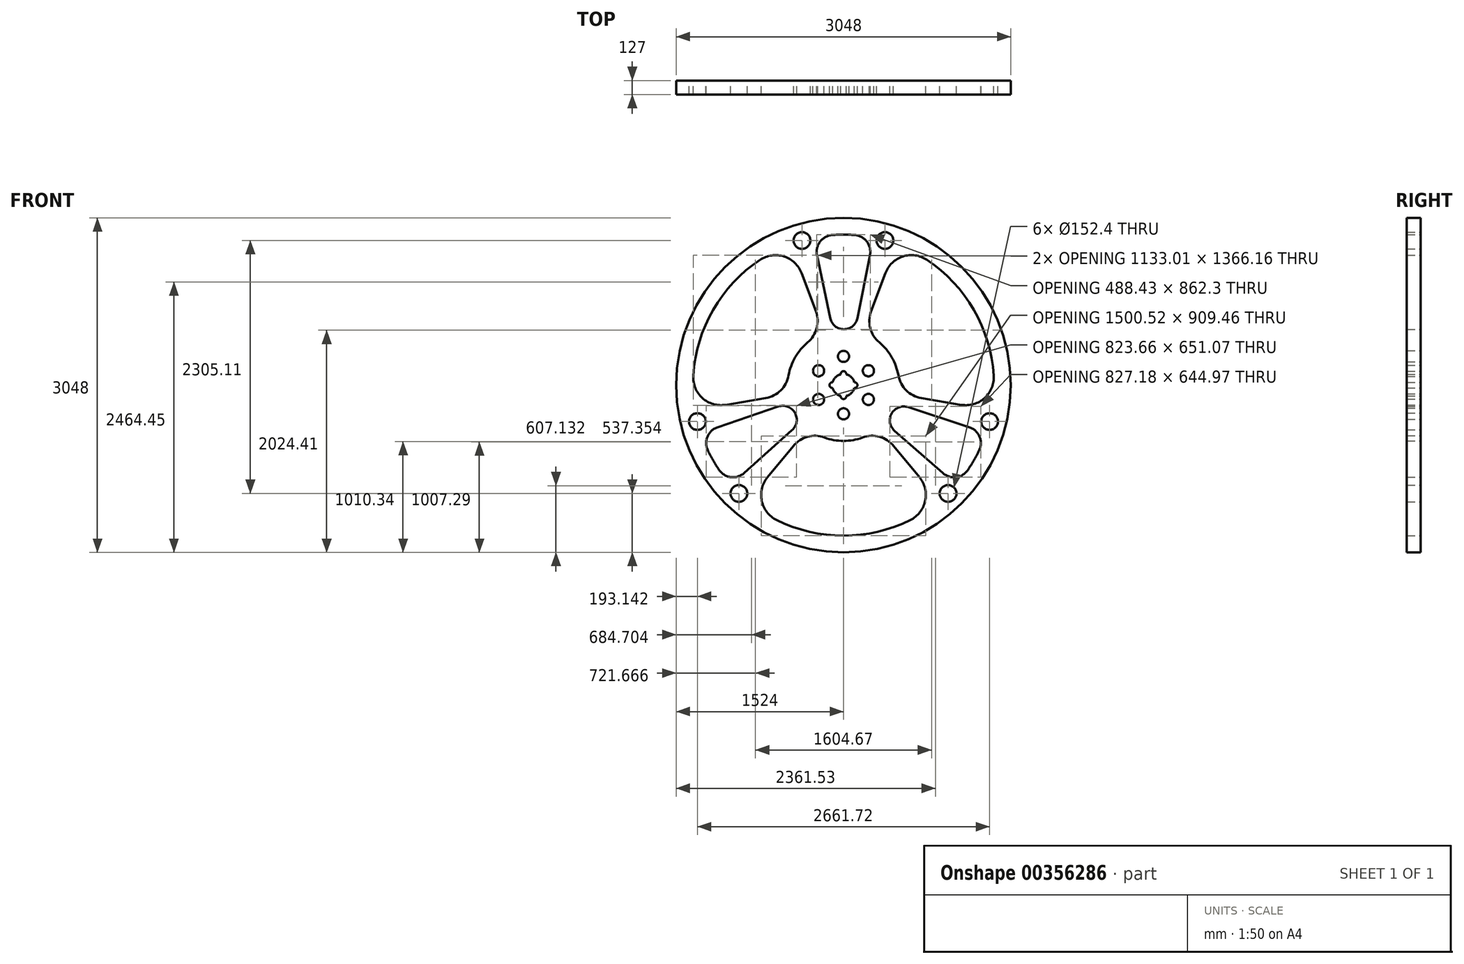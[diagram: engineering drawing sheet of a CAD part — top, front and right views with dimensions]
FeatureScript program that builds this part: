
annotation { "Feature Type Name" : "Feature", "Feature Type Description" : "" }
export const myFeature = defineFeature(function(context is Context, id is Id, definition is map)
    precondition{}
    {
        {
            var Q0;
            Q0=qCreatedBy(makeId("Front.planeOp"),FACE);
            var sketch = newSketch(context, id + "F0", { "sketchPlane" : qUnion([Q0])});
            skCircle(sketch, "E0", {"center": v(0, 0) * mm, "radius": 1524 * mm});
            skCircle(sketch, "E1", {"center": v(0, 0) * mm, "radius": 381 * mm});
            skArc(sketch, "E2", {"start": v(-173.99, -477.28) * mm, "mid": v(0, -508) * mm, "end": v(173.99, -477.28) * mm});
            skArc(sketch, "E3", {"start": v(241.16, 1185.35) * mm, "mid": v(213.39, 1307.65) * mm, "end": v(103.3, 1367.7) * mm});
            skArc(sketch, "E4", {"start": v(-103.3, 1367.7) * mm, "mid": v(-213.39, 1307.65) * mm, "end": v(-241.16, 1185.35) * mm});
            skArc(sketch, "E5", {"start": v(-120.93, 610.98) * mm, "mid": v(3.52, 509.3) * mm, "end": v(127.97, 610.98) * mm});
            skLineSegment(sketch, "E6.trimOffspring", {"start": v(-241.16, 1185.35) * mm, "end": v(-120.93, 610.98) * mm});
            skArc(sketch, "E7.trimOffspring", {"start": v(103.3, 1367.7) * mm, "mid": v(0, 1371.6) * mm, "end": v(-103.3, 1367.7) * mm});
            skLineSegment(sketch, "E8.trimOffspring", {"start": v(241.16, 1185.35) * mm, "end": v(127.97, 610.98) * mm});
            skPoint(sketch, "E9.orphan", {"position": v(0, 1871.22) * mm});
            skPoint(sketch, "E10.start.orphan", {"position": v(380.7, 1871.22) * mm});
            skLineSegment(sketch, "E11.trimOffspring", {"start": v(456.97, -554.35) * mm, "end": v(692.28, -839.8) * mm});
            skLineSegment(sketch, "E12.trimOffspring", {"start": v(-456.97, -554.35) * mm, "end": v(-692.28, -839.8) * mm});
            skArc(sketch, "E13", {"start": v(456.97, -554.35) * mm, "mid": v(327.73, -470.84) * mm, "end": v(173.99, -477.28) * mm});
            skArc(sketch, "E14", {"start": v(-173.99, -477.28) * mm, "mid": v(-327.73, -470.84) * mm, "end": v(-456.97, -554.35) * mm});
            skCircle(sketch, "E15", {"center": v(-378.06, 1318.47) * mm, "radius": 76.2 * mm});
            skCircle(sketch, "E16", {"center": v(378.06, 1318.47) * mm, "radius": 76.2 * mm});
            skArc(sketch, "E17", {"start": v(-609.08, -1228.95) * mm, "mid": v(0, -1371.6) * mm, "end": v(609.08, -1228.95) * mm});
            skArc(sketch, "E18", {"start": v(-692.28, -839.8) * mm, "mid": v(-744.67, -1054.47) * mm, "end": v(-609.08, -1228.95) * mm});
            skArc(sketch, "E19", {"start": v(609.08, -1228.95) * mm, "mid": v(744.67, -1054.47) * mm, "end": v(692.28, -839.8) * mm});
            skArc(sketch, "E20.trimOffspring", {"start": v(1132.82, -773.31) * mm, "mid": v(1187.84, -685.8) * mm, "end": v(1236.12, -594.4) * mm});
            skArc(sketch, "E21.1.0", {"start": v(-1236.12, -594.4) * mm, "mid": v(-1187.84, -685.8) * mm, "end": v(-1132.82, -773.31) * mm});
            skArc(sketch, "E21.1.1", {"start": v(-1132.82, -773.31) * mm, "mid": v(-1025.76, -838.62) * mm, "end": v(-905.96, -801.53) * mm});
            skLineSegment(sketch, "E21.1.2", {"start": v(-905.96, -801.53) * mm, "end": v(-468.66, -410.22) * mm});
            skArc(sketch, "E21.1.3", {"start": v(-468.66, -410.22) * mm, "mid": v(-442.83, -251.6) * mm, "end": v(-593.11, -194.66) * mm});
            skLineSegment(sketch, "E21.1.4", {"start": v(-1147.13, -383.82) * mm, "end": v(-593.11, -194.66) * mm});
            skArc(sketch, "E21.1.5", {"start": v(-1147.13, -383.82) * mm, "mid": v(-1239.15, -469.02) * mm, "end": v(-1236.12, -594.4) * mm});
            skCircle(sketch, "E21.1.6", {"center": v(-1330.86, -331.82) * mm, "radius": 76.2 * mm});
            skCircle(sketch, "E21.1.7", {"center": v(-952.8, -986.65) * mm, "radius": 76.2 * mm});
            skArc(sketch, "E21.2.1", {"start": v(1236.12, -594.4) * mm, "mid": v(1239.15, -469.02) * mm, "end": v(1147.13, -383.82) * mm});
            skLineSegment(sketch, "E21.2.2", {"start": v(1147.13, -383.82) * mm, "end": v(589.59, -200.77) * mm});
            skArc(sketch, "E21.2.3", {"start": v(589.59, -200.77) * mm, "mid": v(439.3, -257.7) * mm, "end": v(465.14, -416.32) * mm});
            skLineSegment(sketch, "E21.2.4", {"start": v(905.96, -801.53) * mm, "end": v(465.14, -416.32) * mm});
            skArc(sketch, "E21.2.5", {"start": v(905.96, -801.53) * mm, "mid": v(1025.76, -838.62) * mm, "end": v(1132.82, -773.31) * mm});
            skCircle(sketch, "E21.2.6", {"center": v(952.8, -986.65) * mm, "radius": 76.2 * mm});
            skCircle(sketch, "E21.2.7", {"center": v(1330.86, -331.82) * mm, "radius": 76.2 * mm});
            skArc(sketch, "E22.1.0", {"start": v(251.6, 672.92) * mm, "mid": v(243.9, 519.24) * mm, "end": v(326.34, 389.31) * mm});
            skArc(sketch, "E22.1.1", {"start": v(500.33, 87.96) * mm, "mid": v(439.94, 254) * mm, "end": v(326.34, 389.31) * mm});
            skArc(sketch, "E22.1.2", {"start": v(500.33, 87.96) * mm, "mid": v(571.62, -48.4) * mm, "end": v(708.57, -118.57) * mm});
            skLineSegment(sketch, "E22.1.3", {"start": v(708.57, -118.57) * mm, "end": v(1073.43, -179.63) * mm});
            skArc(sketch, "E22.1.4", {"start": v(1073.43, -179.63) * mm, "mid": v(1285.53, -117.67) * mm, "end": v(1368.84, 87) * mm});
            skArc(sketch, "E22.1.5", {"start": v(1368.84, 87) * mm, "mid": v(1187.84, 685.8) * mm, "end": v(759.76, 1141.95) * mm});
            skArc(sketch, "E22.1.6", {"start": v(759.76, 1141.95) * mm, "mid": v(540.86, 1172.14) * mm, "end": v(381.15, 1019.43) * mm});
            skLineSegment(sketch, "E22.1.7", {"start": v(251.6, 672.92) * mm, "end": v(381.15, 1019.43) * mm});
            skArc(sketch, "E22.2.0", {"start": v(-708.57, -118.57) * mm, "mid": v(-571.62, -48.4) * mm, "end": v(-500.33, 87.96) * mm});
            skArc(sketch, "E22.2.1", {"start": v(-326.34, 389.31) * mm, "mid": v(-439.94, 254) * mm, "end": v(-500.33, 87.96) * mm});
            skArc(sketch, "E22.2.2", {"start": v(-326.34, 389.31) * mm, "mid": v(-243.9, 519.24) * mm, "end": v(-251.6, 672.92) * mm});
            skLineSegment(sketch, "E22.2.3", {"start": v(-251.6, 672.92) * mm, "end": v(-381.15, 1019.43) * mm});
            skArc(sketch, "E22.2.4", {"start": v(-381.15, 1019.43) * mm, "mid": v(-540.86, 1172.14) * mm, "end": v(-759.76, 1141.95) * mm});
            skArc(sketch, "E22.2.5", {"start": v(-759.76, 1141.95) * mm, "mid": v(-1187.84, 685.8) * mm, "end": v(-1368.84, 87) * mm});
            skArc(sketch, "E22.2.6", {"start": v(-1368.84, 87) * mm, "mid": v(-1285.53, -117.67) * mm, "end": v(-1073.43, -179.63) * mm});
            skLineSegment(sketch, "E22.2.7", {"start": v(-708.57, -118.57) * mm, "end": v(-1073.43, -179.63) * mm});
            skCircle(sketch, "E23", {"center": v(0, 261.86) * mm, "radius": 50.8 * mm});
            skCircle(sketch, "E24.1.0", {"center": v(-226.78, -130.93) * mm, "radius": 50.8 * mm});
            skCircle(sketch, "E24.2.0", {"center": v(226.78, -130.93) * mm, "radius": 50.8 * mm});
            skCircle(sketch, "E25.1.1", {"center": v(0, -261.86) * mm, "radius": 50.8 * mm});
            skCircle(sketch, "E25.1.2", {"center": v(226.78, 130.93) * mm, "radius": 50.8 * mm});
            skCircle(sketch, "E26.4.3.0", {"center": v(-226.78, 130.93) * mm, "radius": 50.8 * mm});
            skCircle(sketch, "E26.2.5.0", {"center": v(-226.78, 130.93) * mm, "radius": 50.8 * mm});
            skArc(sketch, "E27", {"start": v(-25.2, 98.42) * mm, "mid": v(-71.84, 71.84) * mm, "end": v(-98.43, 25.2) * mm});
            skArc(sketch, "E28", {"start": v(-98.43, 25.2) * mm, "mid": v(-127, 0) * mm, "end": v(-98.43, -25.2) * mm});
            skArc(sketch, "E29", {"start": v(98.42, -25.2) * mm, "mid": v(127, 0) * mm, "end": v(98.43, 25.2) * mm});
            skArc(sketch, "E30", {"start": v(25.2, 98.42) * mm, "mid": v(0, 127) * mm, "end": v(-25.2, 98.43) * mm});
            skArc(sketch, "E31", {"start": v(-25.2, -98.42) * mm, "mid": v(0, -127) * mm, "end": v(25.2, -98.43) * mm});
            skArc(sketch, "E32.trimOffspring", {"start": v(98.43, 25.2) * mm, "mid": v(71.84, 71.84) * mm, "end": v(25.2, 98.42) * mm});
            skArc(sketch, "E33.trimOffspring", {"start": v(25.2, -98.42) * mm, "mid": v(71.84, -71.84) * mm, "end": v(98.43, -25.2) * mm});
            skArc(sketch, "E34.trimOffspring", {"start": v(-98.43, -25.2) * mm, "mid": v(-71.84, -71.84) * mm, "end": v(-25.2, -98.42) * mm});
            skSolve(sketch);
        }
        {
            var Q0;
            Q0=makeQuery(id+"F0.imprint","IMPRINT",FACE,{"disambiguationData":[TD([[makeQuery(id+"F0.imprint","IMPRINT",EDGE,{"derivedFrom":sQuery(id+"F0.wireOp",EDGE,"E0")}),1.0]])]});
            var Q1;
            Q1=makeQuery(id+"F0.imprint","IMPRINT",FACE,{"disambiguationData":[TD([[makeQuery(id+"F0.imprint","IMPRINT",EDGE,{"derivedFrom":sQuery(id+"F0.wireOp",EDGE,"E1")}),1.0]])]});
            extrude(context, id + "F1", {"entities" : qUnion([Q0, Q1]), "depth" : 127 * mm});
        }
    });
